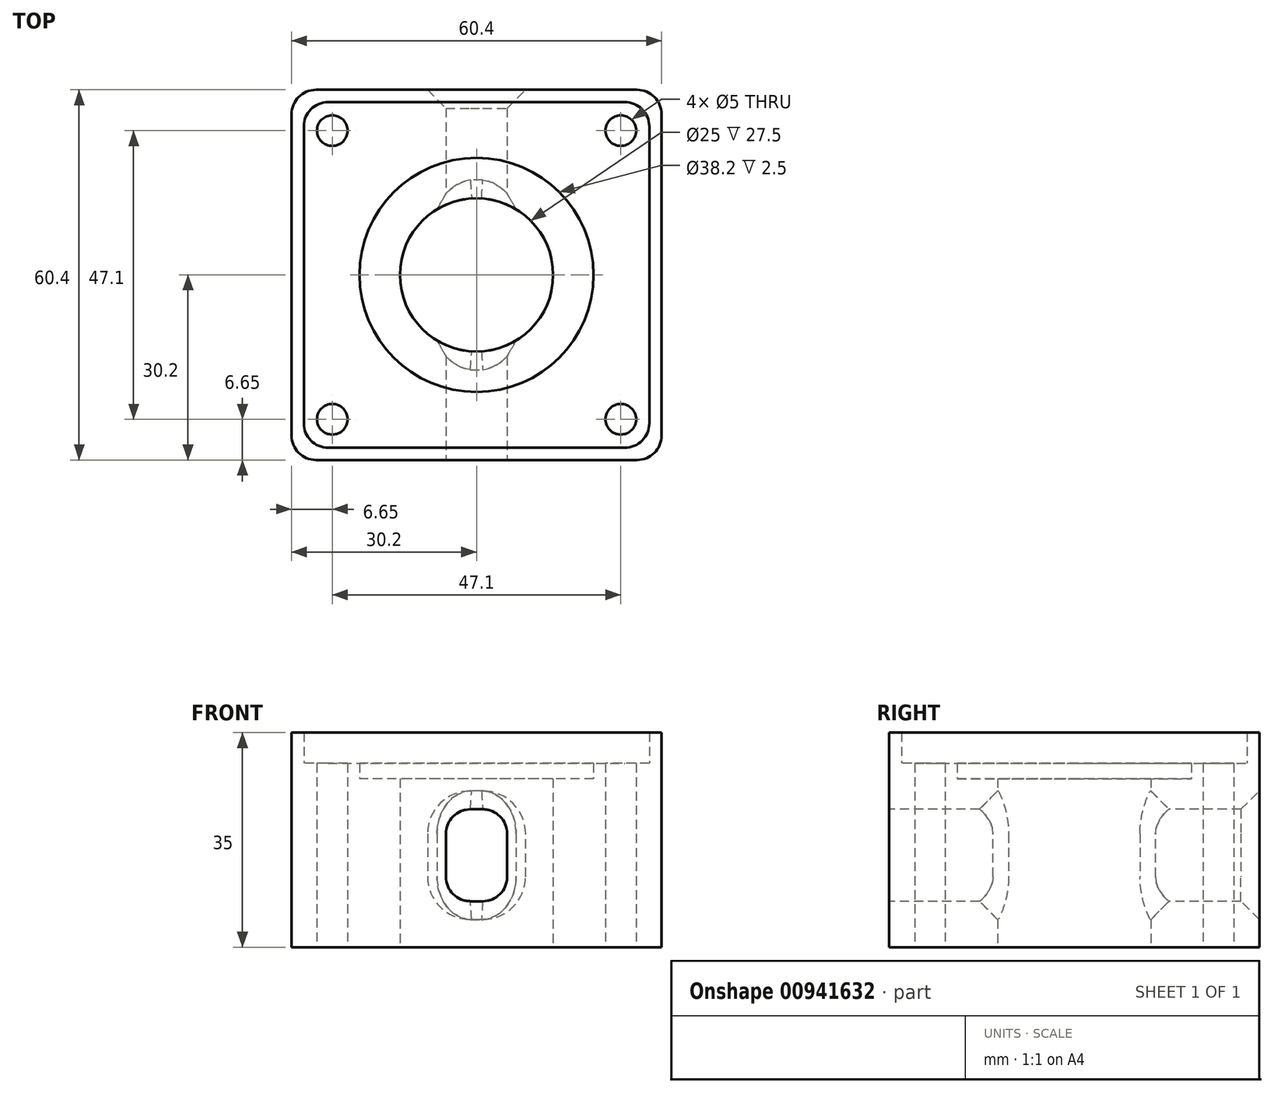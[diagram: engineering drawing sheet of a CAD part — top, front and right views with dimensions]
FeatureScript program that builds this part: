
annotation { "Feature Type Name" : "Feature", "Feature Type Description" : "" }
export const myFeature = defineFeature(function(context is Context, id is Id, definition is map)
    precondition{}
    {
        {
            var Q0;
            Q0=qCreatedBy(makeId("Top.planeOp"),FACE);
            var sketch = newSketch(context, id + "F0", { "sketchPlane" : qUnion([Q0])});
            skCircle(sketch, "E0", {"center": v(0, 0) * mm, "radius": 12.5 * mm});
            skLineSegment(sketch, "E1.bottom", {"start": v(-26.2, -30.2) * mm, "end": v(26.2, -30.2) * mm});
            skLineSegment(sketch, "E1.top", {"start": v(-26.2, 30.2) * mm, "end": v(26.2, 30.2) * mm});
            skLineSegment(sketch, "E1.left", {"start": v(-30.2, -26.2) * mm, "end": v(-30.2, 26.2) * mm});
            skLineSegment(sketch, "E1.right", {"start": v(30.2, -26.2) * mm, "end": v(30.2, 26.2) * mm});
            skLineSegment(sketch, "E2.bottom", {"start": v(-23.55, -23.55) * mm, "end": v(23.55, -23.55) * mm, "construction": true});
            skLineSegment(sketch, "E2.top", {"start": v(-23.55, 23.55) * mm, "end": v(23.55, 23.55) * mm, "construction": true});
            skLineSegment(sketch, "E2.left", {"start": v(-23.55, -23.55) * mm, "end": v(-23.55, 23.55) * mm, "construction": true});
            skLineSegment(sketch, "E2.right", {"start": v(23.55, -23.55) * mm, "end": v(23.55, 23.55) * mm, "construction": true});
            skCircle(sketch, "E3", {"center": v(-23.55, -23.55) * mm, "radius": 2.5 * mm});
            skCircle(sketch, "E4", {"center": v(-23.55, 23.55) * mm, "radius": 2.5 * mm});
            skCircle(sketch, "E5", {"center": v(23.55, 23.55) * mm, "radius": 2.5 * mm});
            skCircle(sketch, "E6", {"center": v(23.55, -23.55) * mm, "radius": 2.5 * mm});
            skLineSegment(sketch, "E7.bottom", {"start": v(-24.2, -28.2) * mm, "end": v(24.2, -28.2) * mm});
            skLineSegment(sketch, "E7.top", {"start": v(-24.2, 28.2) * mm, "end": v(24.2, 28.2) * mm});
            skLineSegment(sketch, "E7.left", {"start": v(-28.2, -24.2) * mm, "end": v(-28.2, 24.2) * mm});
            skLineSegment(sketch, "E7.right", {"start": v(28.2, -24.2) * mm, "end": v(28.2, 24.2) * mm});
            skPoint(sketch, "E8.visualSharp", {"position": v(-28.2, 28.2) * mm});
            skArc(sketch, "E8.filletArc", {"start": v(-24.2, 28.2) * mm, "mid": v(-27.03, 27.03) * mm, "end": v(-28.2, 24.2) * mm});
            skPoint(sketch, "E9.visualSharp", {"position": v(28.2, 28.2) * mm});
            skArc(sketch, "E9.filletArc", {"start": v(28.2, 24.2) * mm, "mid": v(27.03, 27.03) * mm, "end": v(24.2, 28.2) * mm});
            skPoint(sketch, "E10.visualSharp", {"position": v(28.2, -28.2) * mm});
            skArc(sketch, "E10.filletArc", {"start": v(24.2, -28.2) * mm, "mid": v(27.03, -27.03) * mm, "end": v(28.2, -24.2) * mm});
            skPoint(sketch, "E11.visualSharp", {"position": v(-28.2, -28.2) * mm});
            skArc(sketch, "E11.filletArc", {"start": v(-28.2, -24.2) * mm, "mid": v(-27.03, -27.03) * mm, "end": v(-24.2, -28.2) * mm});
            skPoint(sketch, "E12.visualSharp", {"position": v(-30.2, 30.2) * mm});
            skArc(sketch, "E12.filletArc", {"start": v(-26.2, 30.2) * mm, "mid": v(-29.03, 29.03) * mm, "end": v(-30.2, 26.2) * mm});
            skPoint(sketch, "E13.visualSharp", {"position": v(30.2, 30.2) * mm});
            skArc(sketch, "E13.filletArc", {"start": v(30.2, 26.2) * mm, "mid": v(29.03, 29.03) * mm, "end": v(26.2, 30.2) * mm});
            skPoint(sketch, "E14.visualSharp", {"position": v(30.2, -30.2) * mm});
            skArc(sketch, "E14.filletArc", {"start": v(26.2, -30.2) * mm, "mid": v(29.03, -29.03) * mm, "end": v(30.2, -26.2) * mm});
            skPoint(sketch, "E15.visualSharp", {"position": v(-30.2, -30.2) * mm});
            skArc(sketch, "E15.filletArc", {"start": v(-30.2, -26.2) * mm, "mid": v(-29.03, -29.03) * mm, "end": v(-26.2, -30.2) * mm});
            skCircle(sketch, "E16", {"center": v(0, 0) * mm, "radius": 19.1 * mm});
            skSolve(sketch);
        }
        {
            var Q0;
            Q0=makeQuery(id+"F0.imprint","IMPRINT",FACE,{"disambiguationData":[TD([[makeQuery(id+"F0.imprint","IMPRINT",EDGE,{"derivedFrom":sQuery(id+"F0.wireOp",EDGE,"E1.bottom")}),1.0]])]});
            var Q1;
            Q1=makeQuery(id+"F0.imprint","IMPRINT",FACE,{"disambiguationData":[TD([[makeQuery(id+"F0.imprint","IMPRINT",EDGE,{"derivedFrom":sQuery(id+"F0.wireOp",EDGE,"E3")}),-1.0]])]});
            var Q2;
            Q2=makeQuery(id+"F0.imprint","IMPRINT",FACE,{"disambiguationData":[TD([[makeQuery(id+"F0.imprint","IMPRINT",EDGE,{"derivedFrom":sQuery(id+"F0.wireOp",EDGE,"E0")}),-1.0]])]});
            extrude(context, id + "F1", {"entities" : qUnion([Q0, Q1, Q2]), "depth" : 30 * mm, "offsetDistance" : 25 * mm});
        }
        {
            var Q0;
            Q0=makeQuery(id+"F0.imprint","IMPRINT",FACE,{"disambiguationData":[TD([[makeQuery(id+"F0.imprint","IMPRINT",EDGE,{"derivedFrom":sQuery(id+"F0.wireOp",EDGE,"E1.bottom")}),1.0]])]});
            extrude(context, id + "F2", {"entities" : qUnion([Q0]), "operationType" : NewBodyOperationType.ADD, "depth" : 35 * mm, "offsetDistance" : 25 * mm, "hasSecondDirection" : true, "secondDirectionOppositeDirection" : false, "secondDirectionDepth" : 30 * mm});
        }
        {
            var Q0;
            Q0=makeQuery(id+"F0.imprint","IMPRINT",FACE,{"disambiguationData":[TD([[makeQuery(id+"F0.imprint","IMPRINT",EDGE,{"derivedFrom":sQuery(id+"F0.wireOp",EDGE,"E0")}),-1.0]])]});
            extrude(context, id + "F3", {"entities" : qUnion([Q0]), "operationType" : NewBodyOperationType.REMOVE, "depth" : 30 * mm, "offsetDistance" : 25 * mm, "hasSecondDirection" : true, "secondDirectionOppositeDirection" : false, "secondDirectionDepth" : 27.5 * mm});
        }
        {
            var Q0;
            {var subQ0=sQuery(id+"F0.wireOp",EDGE,"E1.bottom");Q0=makeQuery(id+"F2.boolean.opBoolean","MERGE",FACE,{"derivedFrom":[makeQuery(id+"F1.opExtrude","SWEPT_FACE",FACE,{"disambiguationData":[OSD([subQ0])]}),makeQuery(id+"F2.opExtrude","SWEPT_FACE",FACE,{"disambiguationData":[OSD([subQ0])]})]});}
            var sketch = newSketch(context, id + "F4", { "sketchPlane" : qUnion([Q0])});
            skLineSegment(sketch, "E17.bottom", {"start": v(-1, 7.5) * mm, "end": v(1, 7.5) * mm});
            skLineSegment(sketch, "E17.top", {"start": v(-1, 22.5) * mm, "end": v(1, 22.5) * mm});
            skLineSegment(sketch, "E17.left", {"start": v(-5, 11.5) * mm, "end": v(-5, 18.5) * mm});
            skLineSegment(sketch, "E17.right", {"start": v(5, 11.5) * mm, "end": v(5, 18.5) * mm});
            skPoint(sketch, "E17.middle", {"position": v(0, 15) * mm});
            skPoint(sketch, "E18.visualSharp", {"position": v(-5, 22.5) * mm});
            skArc(sketch, "E18.filletArc", {"start": v(-1, 22.5) * mm, "mid": v(-3.83, 21.33) * mm, "end": v(-5, 18.5) * mm});
            skPoint(sketch, "E19.visualSharp", {"position": v(5, 22.5) * mm});
            skArc(sketch, "E19.filletArc", {"start": v(5, 18.5) * mm, "mid": v(3.83, 21.33) * mm, "end": v(1, 22.5) * mm});
            skPoint(sketch, "E20.visualSharp", {"position": v(5, 7.5) * mm});
            skArc(sketch, "E20.filletArc", {"start": v(1, 7.5) * mm, "mid": v(3.83, 8.67) * mm, "end": v(5, 11.5) * mm});
            skPoint(sketch, "E21.visualSharp", {"position": v(-5, 7.5) * mm});
            skArc(sketch, "E21.filletArc", {"start": v(-5, 11.5) * mm, "mid": v(-3.83, 8.67) * mm, "end": v(-1, 7.5) * mm});
            skSolve(sketch);
        }
        {
            var Q0;
            Q0=makeQuery(id+"F4.imprint","IMPRINT",FACE,{"disambiguationData":[TD([[makeQuery(id+"F4.imprint","IMPRINT",EDGE,{"derivedFrom":sQuery(id+"F4.wireOp",EDGE,"E17.bottom")}),1.0]])]});
            var Q1;
            Q1 = qConstructionFilter(qBodyType(qCreatedBy(id + "F4" ,EDGE), BodyType.WIRE), ConstructionObject.NO);
            extrude(context, id + "F5", {"entities" : qUnion([Q0]), "operationType" : NewBodyOperationType.REMOVE, "surfaceEntities" : qUnion([Q1]), "endBound" : BoundingType.THROUGH_ALL, "oppositeDirection" : true, "depth" : 25 * mm, "offsetDistance" : 25 * mm});
        }
        {
            var Q0;
            Q0=makeQuery(id+"F5.boolean.opBoolean","COPY",EDGE,{"derivedFrom":makeQuery(id+"F5.opExtrude","CAP_EDGE",EDGE,{"disambiguationData":[OSD([sQuery(id+"F4.wireOp",EDGE,"E19.filletArc")])],"isStart":true})});
            var Q1;
            Q1=makeQuery(id+"F5.boolean.opBoolean","INTERSECT",EDGE,{"disambiguationData":[OD(0.0)],"derivedFrom":[makeQuery(id+"F1.opExtrude","SWEPT_FACE",FACE,{"disambiguationData":[OSD([sQuery(id+"F0.wireOp",EDGE,"E0")])]}),makeQuery(id+"F5.opExtrude","SWEPT_FACE",FACE,{"disambiguationData":[OSD([sQuery(id+"F4.wireOp",EDGE,"E17.left")])]})]});
            var Q2;
            {var subQ0=sQuery(id+"F0.wireOp",EDGE,"E1.top");Q2=makeQuery(id+"F5.boolean.opBoolean","INTERSECT",EDGE,{"derivedFrom":[makeQuery(id+"F2.boolean.opBoolean","MERGE",FACE,{"derivedFrom":[makeQuery(id+"F1.opExtrude","SWEPT_FACE",FACE,{"disambiguationData":[OSD([subQ0])]}),makeQuery(id+"F2.opExtrude","SWEPT_FACE",FACE,{"disambiguationData":[OSD([subQ0])]})]}),makeQuery(id+"F5.opExtrude","SWEPT_FACE",FACE,{"disambiguationData":[OSD([sQuery(id+"F4.wireOp",EDGE,"E18.filletArc")])]})]});}
            var Q3;
            Q3=makeQuery(id+"F5.boolean.opBoolean","INTERSECT",EDGE,{"disambiguationData":[OD(1.0)],"derivedFrom":[makeQuery(id+"F1.opExtrude","SWEPT_FACE",FACE,{"disambiguationData":[OSD([sQuery(id+"F0.wireOp",EDGE,"E0")])]}),makeQuery(id+"F5.opExtrude","SWEPT_FACE",FACE,{"disambiguationData":[OSD([sQuery(id+"F4.wireOp",EDGE,"E17.left")])]})]});
            chamfer(context, id + "F6", {"entities" : qUnion([Q0, Q1, Q2, Q3]), "width" : 3 * mm, "tangentPropagation" : true});
        }
    });
